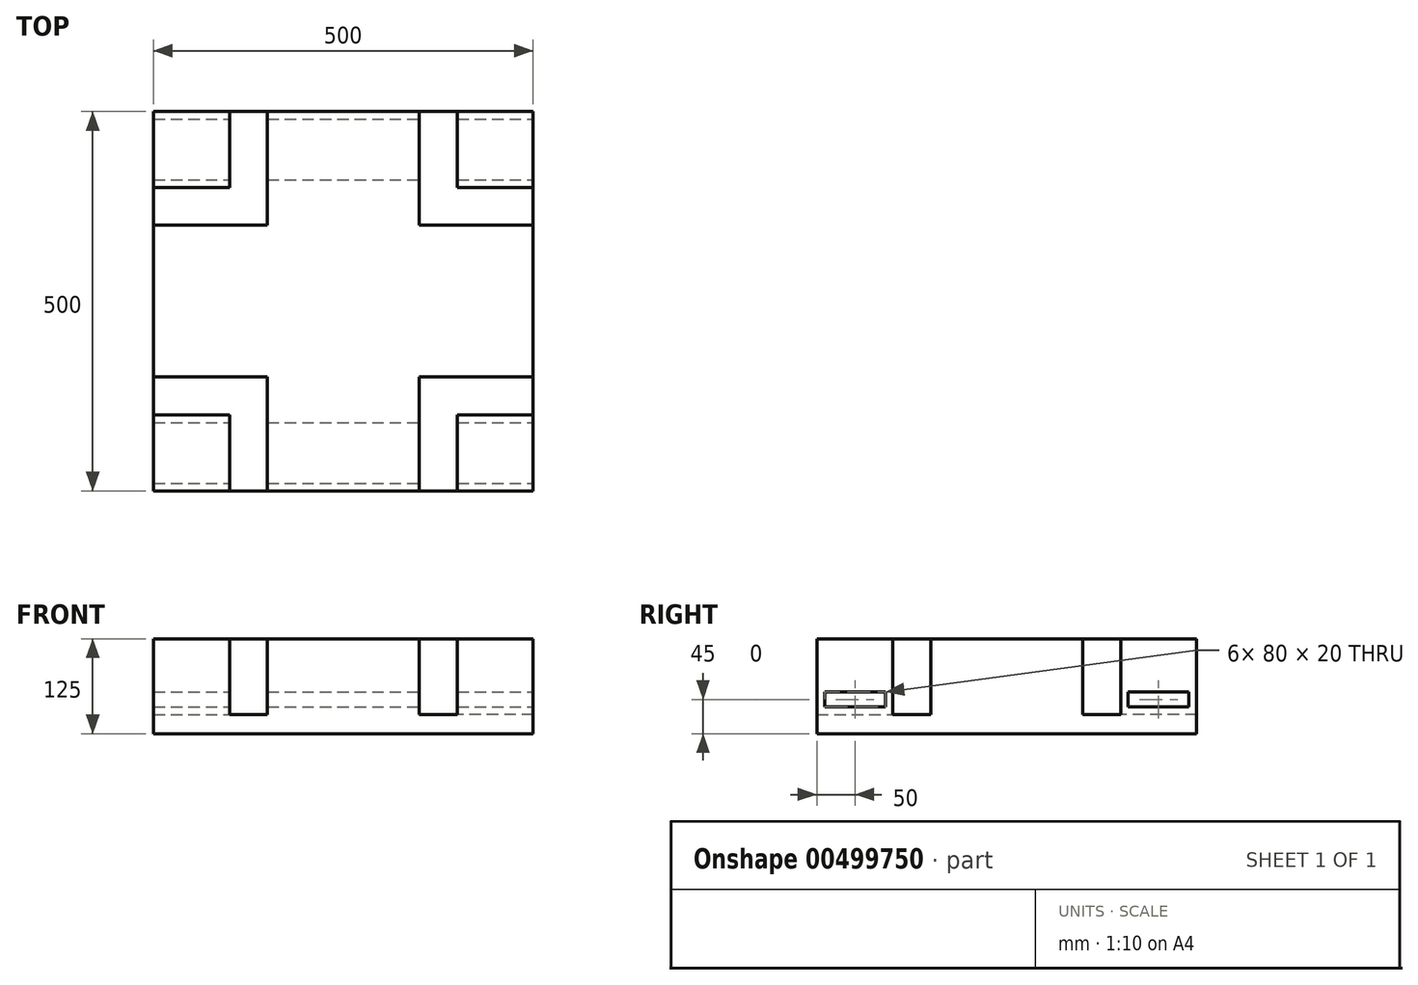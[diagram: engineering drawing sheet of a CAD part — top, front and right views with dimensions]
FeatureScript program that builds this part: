
annotation { "Feature Type Name" : "Feature", "Feature Type Description" : "" }
export const myFeature = defineFeature(function(context is Context, id is Id, definition is map)
    precondition{}
    {
        {
            var Q0;
            Q0=qCreatedBy(makeId("Top.planeOp"),FACE);
            var sketch = newSketch(context, id + "F0", { "sketchPlane" : qUnion([Q0])});
            skLineSegment(sketch, "E0.bottom", {"start": v(250, 250) * mm, "end": v(-250, 250) * mm});
            skLineSegment(sketch, "E0.top", {"start": v(250, -250) * mm, "end": v(-250, -250) * mm});
            skLineSegment(sketch, "E0.left", {"start": v(250, 250) * mm, "end": v(250, -250) * mm});
            skLineSegment(sketch, "E0.right", {"start": v(-250, 250) * mm, "end": v(-250, -250) * mm});
            skPoint(sketch, "E0.middle", {"position": v(0, 0) * mm});
            skLineSegment(sketch, "E1.top", {"start": v(-250, 150) * mm, "end": v(-150, 150) * mm});
            skLineSegment(sketch, "E1.right", {"start": v(-150, 250) * mm, "end": v(-150, 150) * mm});
            skLineSegment(sketch, "E2.bottom", {"start": v(-250, 250) * mm, "end": v(-100, 250) * mm});
            skLineSegment(sketch, "E2.top", {"start": v(-250, 100) * mm, "end": v(-100, 100) * mm});
            skLineSegment(sketch, "E2.left", {"start": v(-250, 250) * mm, "end": v(-250, 100) * mm});
            skLineSegment(sketch, "E2.right", {"start": v(-100, 250) * mm, "end": v(-100, 100) * mm});
            skLineSegment(sketch, "E3", {"start": v(-250, 0) * mm, "end": v(250, 0) * mm, "construction": true});
            skLineSegment(sketch, "E4", {"start": v(0, 250) * mm, "end": v(0, -250) * mm, "construction": true});
            skLineSegment(sketch, "E5.MirrorCS", {"start": v(250, 100) * mm, "end": v(100, 100) * mm});
            skLineSegment(sketch, "E6.MirrorCS", {"start": v(250, 150) * mm, "end": v(150, 150) * mm});
            skLineSegment(sketch, "E7.MirrorCS", {"start": v(150, 250) * mm, "end": v(150, 150) * mm});
            skLineSegment(sketch, "E8.MirrorCS", {"start": v(100, 250) * mm, "end": v(100, 100) * mm});
            skLineSegment(sketch, "E9.MirrorCS", {"start": v(-250, -100) * mm, "end": v(-100, -100) * mm});
            skLineSegment(sketch, "E10.MirrorCS", {"start": v(-250, -150) * mm, "end": v(-150, -150) * mm});
            skLineSegment(sketch, "E11.MirrorCS", {"start": v(-150, -250) * mm, "end": v(-150, -150) * mm});
            skLineSegment(sketch, "E12.MirrorCS", {"start": v(-100, -250) * mm, "end": v(-100, -100) * mm});
            skLineSegment(sketch, "E13.MirrorCS", {"start": v(100, -250) * mm, "end": v(100, -100) * mm});
            skLineSegment(sketch, "E14.MirrorCS", {"start": v(250, -100) * mm, "end": v(100, -100) * mm});
            skLineSegment(sketch, "E15.MirrorCS", {"start": v(250, -150) * mm, "end": v(150, -150) * mm});
            skLineSegment(sketch, "E16.MirrorCS", {"start": v(150, -250) * mm, "end": v(150, -150) * mm});
            skSolve(sketch);
        }
        {
            var Q0;
            {var subQ5=sQuery(id+"F0.wireOp",EDGE,"E2.top");Q0=makeQuery(id+"F0.imprint","IMPRINT",FACE,{"disambiguationData":[TD([[makeQuery(id+"F0.imprint","IMPRINT",EDGE,{"derivedFrom":subQ5}),-1.0]])]});}
            var Q1;
            {var subQ4=sQuery(id+"F0.wireOp",EDGE,"E10.MirrorCS");Q1=makeQuery(id+"F0.imprint","IMPRINT",FACE,{"disambiguationData":[TD([[makeQuery(id+"F0.imprint","IMPRINT",EDGE,{"derivedFrom":subQ4}),-1.0]])]});}
            var Q2;
            {var subQ4=sQuery(id+"F0.wireOp",EDGE,"E15.MirrorCS");Q2=makeQuery(id+"F0.imprint","IMPRINT",FACE,{"disambiguationData":[TD([[makeQuery(id+"F0.imprint","IMPRINT",EDGE,{"derivedFrom":subQ4}),1.0]])]});}
            var Q3;
            {var subQ4=sQuery(id+"F0.wireOp",EDGE,"E6.MirrorCS");Q3=makeQuery(id+"F0.imprint","IMPRINT",FACE,{"disambiguationData":[TD([[makeQuery(id+"F0.imprint","IMPRINT",EDGE,{"derivedFrom":subQ4}),-1.0]])]});}
            var Q4;
            {var subQ0=sQuery(id+"F0.wireOp",EDGE,"E1.top");Q4=makeQuery(id+"F0.imprint","IMPRINT",FACE,{"disambiguationData":[TD([[makeQuery(id+"F0.imprint","IMPRINT",EDGE,{"derivedFrom":subQ0}),1.0]])]});}
            extrude(context, id + "F1", {"entities" : qUnion([Q0, Q1, Q2, Q3, Q4]), "depth" : 100 * mm, "offsetDistance" : 25 * mm});
        }
        {
            var Q0;
            {var subQ4=sQuery(id+"F0.wireOp",EDGE,"E15.MirrorCS");Q0=makeQuery(id+"F0.imprint","IMPRINT",FACE,{"disambiguationData":[TD([[makeQuery(id+"F0.imprint","IMPRINT",EDGE,{"derivedFrom":subQ4}),1.0]])]});}
            var Q1;
            {var subQ3=sQuery(id+"F0.wireOp",EDGE,"E13.MirrorCS");Q1=makeQuery(id+"F0.imprint","IMPRINT",FACE,{"disambiguationData":[TD([[makeQuery(id+"F0.imprint","IMPRINT",EDGE,{"derivedFrom":subQ3}),-1.0]])]});}
            var Q2;
            {var subQ1=sQuery(id+"F0.wireOp",EDGE,"E5.MirrorCS");Q2=makeQuery(id+"F0.imprint","IMPRINT",FACE,{"disambiguationData":[TD([[makeQuery(id+"F0.imprint","IMPRINT",EDGE,{"derivedFrom":subQ1}),-1.0]])]});}
            var Q3;
            {var subQ4=sQuery(id+"F0.wireOp",EDGE,"E6.MirrorCS");Q3=makeQuery(id+"F0.imprint","IMPRINT",FACE,{"disambiguationData":[TD([[makeQuery(id+"F0.imprint","IMPRINT",EDGE,{"derivedFrom":subQ4}),-1.0]])]});}
            var Q4;
            {var subQ5=sQuery(id+"F0.wireOp",EDGE,"E2.top");Q4=makeQuery(id+"F0.imprint","IMPRINT",FACE,{"disambiguationData":[TD([[makeQuery(id+"F0.imprint","IMPRINT",EDGE,{"derivedFrom":subQ5}),-1.0]])]});}
            var Q5;
            {var subQ0=sQuery(id+"F0.wireOp",EDGE,"E9.MirrorCS");Q5=makeQuery(id+"F0.imprint","IMPRINT",FACE,{"disambiguationData":[TD([[makeQuery(id+"F0.imprint","IMPRINT",EDGE,{"derivedFrom":subQ0}),-1.0]])]});}
            var Q6;
            {var subQ4=sQuery(id+"F0.wireOp",EDGE,"E10.MirrorCS");Q6=makeQuery(id+"F0.imprint","IMPRINT",FACE,{"disambiguationData":[TD([[makeQuery(id+"F0.imprint","IMPRINT",EDGE,{"derivedFrom":subQ4}),-1.0]])]});}
            var Q7;
            {var subQ4=sQuery(id+"F0.wireOp",EDGE,"E1.top");Q7=makeQuery(id+"F0.imprint","IMPRINT",FACE,{"disambiguationData":[TD([[makeQuery(id+"F0.imprint","IMPRINT",EDGE,{"derivedFrom":subQ4}),-1.0]])]});}
            var Q8;
            {var subQ0=sQuery(id+"F0.wireOp",EDGE,"E1.top");Q8=makeQuery(id+"F0.imprint","IMPRINT",FACE,{"disambiguationData":[TD([[makeQuery(id+"F0.imprint","IMPRINT",EDGE,{"derivedFrom":subQ0}),1.0]])]});}
            extrude(context, id + "F2", {"entities" : qUnion([Q0, Q1, Q2, Q3, Q4, Q5, Q6, Q7, Q8]), "operationType" : NewBodyOperationType.ADD, "oppositeDirection" : true, "depth" : 25 * mm, "offsetDistance" : 25 * mm});
        }
        {
            var Q0;
            {var subQ0=sQuery(id+"F0.wireOp",EDGE,"E0.left");Q0=makeQuery(id+"F2.boolean.opBoolean","MERGE",FACE,{"derivedFrom":[makeQuery(id+"F1.opExtrude","SWEPT_FACE",FACE,{"disambiguationData":[OSD([subQ0]),TDD([makeQuery(id+"F0.imprint","IMPRINT",EDGE,{"disambiguationData":[TD([[makeQuery(id+"F0.imprint","INTERSECT",VERTEX,{"derivedFrom":[sQuery(id+"F0.wireOp",EDGE,"E0.bottom"),subQ0]}),-1.0]])],"derivedFrom":subQ0})])]}),makeQuery(id+"F1.opExtrude","SWEPT_FACE",FACE,{"disambiguationData":[OSD([subQ0]),TDD([makeQuery(id+"F0.imprint","IMPRINT",EDGE,{"disambiguationData":[TD([[makeQuery(id+"F0.imprint","INTERSECT",VERTEX,{"derivedFrom":[subQ0,sQuery(id+"F0.wireOp",EDGE,"E5.MirrorCS")]}),-1.0]])],"derivedFrom":subQ0})])]}),makeQuery(id+"F1.opExtrude","SWEPT_FACE",FACE,{"disambiguationData":[OSD([subQ0]),TDD([makeQuery(id+"F0.imprint","IMPRINT",EDGE,{"disambiguationData":[TD([[makeQuery(id+"F0.imprint","INTERSECT",VERTEX,{"derivedFrom":[sQuery(id+"F0.wireOp",EDGE,"E0.top"),subQ0]}),1.0]])],"derivedFrom":subQ0})])]}),makeQuery(id+"F2.opExtrude","SWEPT_FACE",FACE,{"disambiguationData":[OSD([subQ0])]})]});}
            var sketch = newSketch(context, id + "F3", { "sketchPlane" : qUnion([Q0])});
            skLineSegment(sketch, "E17", {"start": v(0, 0) * mm, "end": v(0, 100) * mm, "construction": true});
            skLineSegment(sketch, "E18.bottom", {"start": v(-240, 30) * mm, "end": v(-160, 30) * mm});
            skLineSegment(sketch, "E18.top", {"start": v(-240, 10) * mm, "end": v(-160, 10) * mm});
            skLineSegment(sketch, "E18.left", {"start": v(-240, 30) * mm, "end": v(-240, 10) * mm});
            skLineSegment(sketch, "E18.right", {"start": v(-160, 30) * mm, "end": v(-160, 10) * mm});
            skLineSegment(sketch, "E19.MirrorCS", {"start": v(160, 30) * mm, "end": v(160, 10) * mm});
            skLineSegment(sketch, "E20.MirrorCS", {"start": v(240, 30) * mm, "end": v(240, 10) * mm});
            skLineSegment(sketch, "E21.MirrorCS", {"start": v(240, 30) * mm, "end": v(160, 30) * mm});
            skLineSegment(sketch, "E22.MirrorCS", {"start": v(240, 10) * mm, "end": v(160, 10) * mm});
            skPoint(sketch, "E23.MirrorCS.end.orphan", {"position": v(-320, 30) * mm});
            skPoint(sketch, "E23.MirrorCS.start.orphan", {"position": v(-240, 30) * mm});
            skPoint(sketch, "E24.MirrorCS.end.orphan", {"position": v(-320, 10) * mm});
            skSolve(sketch);
        }
        {
            var Q0;
            Q0=makeQuery(id+"F3.imprint","IMPRINT",FACE,{"disambiguationData":[TD([[makeQuery(id+"F3.imprint","IMPRINT",EDGE,{"derivedFrom":sQuery(id+"F3.wireOp",EDGE,"E18.bottom")}),-1.0]])]});
            var Q1;
            Q1=makeQuery(id+"F3.imprint","IMPRINT",FACE,{"disambiguationData":[TD([[makeQuery(id+"F3.imprint","IMPRINT",EDGE,{"derivedFrom":sQuery(id+"F3.wireOp",EDGE,"E19.MirrorCS")}),1.0]])]});
            extrude(context, id + "F4", {"entities" : qUnion([Q0, Q1]), "operationType" : NewBodyOperationType.REMOVE, "oppositeDirection" : true, "depth" : 5000 * mm, "offsetDistance" : 25 * mm});
        }
    });
